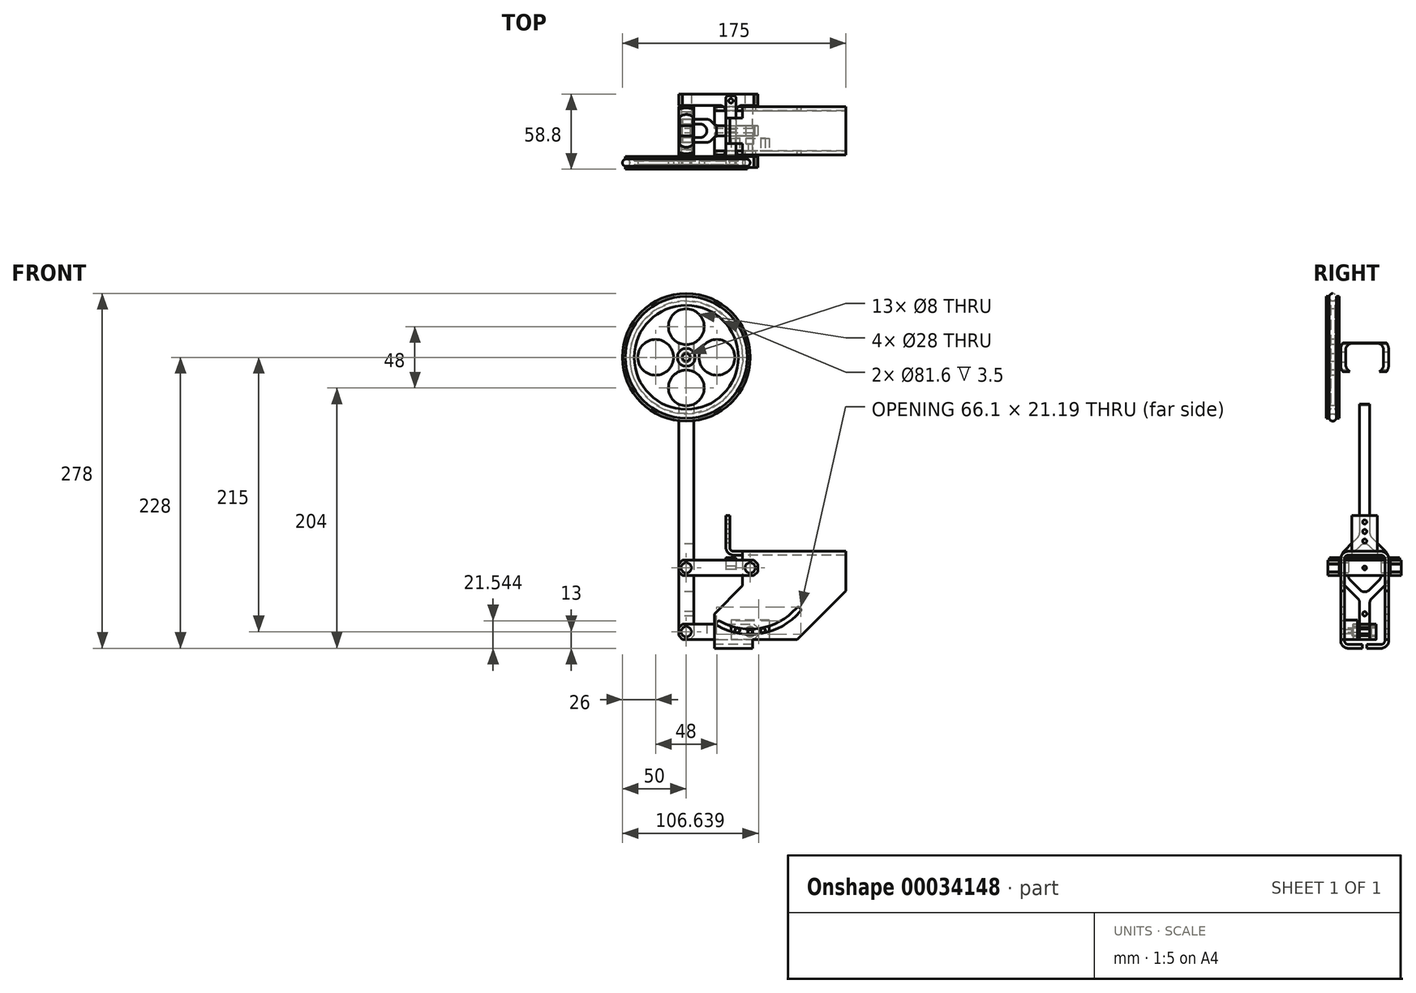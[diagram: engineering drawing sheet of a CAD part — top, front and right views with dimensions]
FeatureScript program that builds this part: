
annotation { "Feature Type Name" : "Feature", "Feature Type Description" : "" }
export const myFeature = defineFeature(function(context is Context, id is Id, definition is map)
    precondition{}
    {
        {
            var Q0;
            Q0=qCreatedBy(makeId("Front.planeOp"),FACE);
            var sketch = newSketch(context, id + "F0", { "sketchPlane" : qUnion([Q0])});
            skLineSegment(sketch, "E0", {"start": v(-68.67, 10) * mm, "end": v(234.98, 10) * mm, "construction": true});
            skLineSegment(sketch, "E1", {"start": v(-69.89, 215) * mm, "end": v(223.35, 215) * mm, "construction": true});
            skLineSegment(sketch, "E2", {"start": v(-65.6, 165) * mm, "end": v(222.13, 165) * mm, "construction": true});
            skLineSegment(sketch, "E3", {"start": v(-66.2, -63) * mm, "end": v(240.7, -63) * mm, "construction": true});
            skSolve(sketch);
        }
        {
            var Q0;
            Q0=sQuery(id+"F0.wireOp",EDGE,"E2");
            cPlane(context, id + "F1", {"entities" : qUnion([Q0]), "cplaneType" : CPlaneType.LINE_ANGLE, "offset" : 370 * mm, "angle" : 90 * degree, "width" : 150 * mm, "height" : 150 * mm});
        }
        {
            var Q0;
            Q0=qCreatedBy(makeId("Right.planeOp"),FACE);
            var sketch = newSketch(context, id + "F2", { "sketchPlane" : qUnion([Q0])});
            skLineSegment(sketch, "E4.bottom", {"start": v(-18.8, 165) * mm, "end": v(18.8, 165) * mm, "construction": true});
            skLineSegment(sketch, "E4.top", {"start": v(-18.8, -50) * mm, "end": v(18.8, -50) * mm, "construction": true});
            skLineSegment(sketch, "E4.left", {"start": v(-18.8, 165) * mm, "end": v(-18.8, -50) * mm, "construction": true});
            skLineSegment(sketch, "E4.right", {"start": v(18.8, 165) * mm, "end": v(18.8, -50) * mm, "construction": true});
            skLineSegment(sketch, "E5", {"start": v(-18.8, 0) * mm, "end": v(18.8, 0) * mm, "construction": true});
            skLineSegment(sketch, "E6", {"start": v(16.16, 152.64) * mm, "end": v(5.46, 141.94) * mm});
            skLineSegment(sketch, "E7", {"start": v(4, 138.4) * mm, "end": v(4, 27.43) * mm});
            skLineSegment(sketch, "E8", {"start": v(5.46, 23.9) * mm, "end": v(15.58, 13.78) * mm});
            skLineSegment(sketch, "E9", {"start": v(18.8, 6) * mm, "end": v(18.8, -6) * mm});
            skLineSegment(sketch, "E10", {"start": v(15.58, -13.78) * mm, "end": v(5.46, -23.9) * mm});
            skLineSegment(sketch, "E11", {"start": v(4, -27.43) * mm, "end": v(4, -50) * mm});
            skLineSegment(sketch, "E12", {"start": v(13.34, 155.46) * mm, "end": v(3.54, 145.66) * mm});
            skLineSegment(sketch, "E13", {"start": v(3.54, 17.34) * mm, "end": v(11.34, 9.54) * mm});
            skLineSegment(sketch, "E14", {"start": v(12.8, 6) * mm, "end": v(12.8, -6) * mm});
            skLineSegment(sketch, "E15", {"start": v(11.34, -9.54) * mm, "end": v(3.54, -17.34) * mm});
            skArc(sketch, "E16.filletArc", {"start": v(13.34, 155.46) * mm, "mid": v(14.42, 157.09) * mm, "end": v(14.8, 159) * mm});
            skPoint(sketch, "E17.visualSharp", {"position": v(18.8, 155.27) * mm});
            skArc(sketch, "E17.filletArc", {"start": v(16.16, 152.64) * mm, "mid": v(18.11, 155.56) * mm, "end": v(18.8, 159) * mm});
            skPoint(sketch, "E18.visualSharp", {"position": v(4, 140.47) * mm});
            skArc(sketch, "E18.filletArc", {"start": v(5.46, 141.94) * mm, "mid": v(4.38, 140.31) * mm, "end": v(4, 138.4) * mm});
            skPoint(sketch, "E19.visualSharp", {"position": v(4, 25.36) * mm});
            skArc(sketch, "E19.filletArc", {"start": v(4, 27.43) * mm, "mid": v(4.38, 25.51) * mm, "end": v(5.46, 23.9) * mm});
            skPoint(sketch, "E20.visualSharp", {"position": v(18.8, 10.56) * mm});
            skArc(sketch, "E20.filletArc", {"start": v(18.8, 6) * mm, "mid": v(17.96, 10.2) * mm, "end": v(15.58, 13.78) * mm});
            skPoint(sketch, "E21.visualSharp", {"position": v(18.8, -10.56) * mm});
            skArc(sketch, "E21.filletArc", {"start": v(15.58, -13.78) * mm, "mid": v(17.96, -10.2) * mm, "end": v(18.8, -6) * mm});
            skPoint(sketch, "E22.visualSharp", {"position": v(4, -25.36) * mm});
            skArc(sketch, "E22.filletArc", {"start": v(5.46, -23.9) * mm, "mid": v(4.38, -25.51) * mm, "end": v(4, -27.43) * mm});
            skPoint(sketch, "E23.visualSharp", {"position": v(12.8, 8.07) * mm});
            skArc(sketch, "E23.filletArc", {"start": v(12.8, 6) * mm, "mid": v(12.42, 7.91) * mm, "end": v(11.34, 9.54) * mm});
            skPoint(sketch, "E24.visualSharp", {"position": v(12.8, -8.07) * mm});
            skArc(sketch, "E24.filletArc", {"start": v(11.34, -9.54) * mm, "mid": v(12.42, -7.91) * mm, "end": v(12.8, -6) * mm});
            skLineSegment(sketch, "E25.MirrorCS", {"start": v(-13.34, 155.46) * mm, "end": v(-3.54, 145.66) * mm});
            skArc(sketch, "E26.MirrorCS", {"start": v(-13.34, 155.46) * mm, "mid": v(-14.42, 157.09) * mm, "end": v(-14.8, 159) * mm});
            skLineSegment(sketch, "E27.MirrorCS", {"start": v(-16.16, 152.64) * mm, "end": v(-5.46, 141.94) * mm});
            skArc(sketch, "E28.MirrorCS", {"start": v(-5.46, 141.94) * mm, "mid": v(-4.38, 140.31) * mm, "end": v(-4, 138.4) * mm});
            skLineSegment(sketch, "E29.MirrorCS", {"start": v(-4, 138.4) * mm, "end": v(-4, 27.43) * mm});
            skArc(sketch, "E30.MirrorCS", {"start": v(-4, 27.43) * mm, "mid": v(-4.38, 25.51) * mm, "end": v(-5.46, 23.9) * mm});
            skLineSegment(sketch, "E31.MirrorCS", {"start": v(-5.46, 23.9) * mm, "end": v(-15.58, 13.78) * mm});
            skArc(sketch, "E32.MirrorCS", {"start": v(-18.8, 6) * mm, "mid": v(-17.96, 10.2) * mm, "end": v(-15.58, 13.78) * mm});
            skLineSegment(sketch, "E33.MirrorCS", {"start": v(-18.8, 6) * mm, "end": v(-18.8, -6) * mm});
            skArc(sketch, "E34.MirrorCS", {"start": v(-15.58, -13.78) * mm, "mid": v(-17.96, -10.2) * mm, "end": v(-18.8, -6) * mm});
            skLineSegment(sketch, "E35.MirrorCS", {"start": v(-15.58, -13.78) * mm, "end": v(-5.46, -23.9) * mm});
            skArc(sketch, "E36.MirrorCS", {"start": v(-5.46, -23.9) * mm, "mid": v(-4.38, -25.51) * mm, "end": v(-4, -27.43) * mm});
            skLineSegment(sketch, "E37.MirrorCS", {"start": v(-4, -27.43) * mm, "end": v(-4, -50) * mm});
            skLineSegment(sketch, "E38.MirrorCS", {"start": v(-11.34, -9.54) * mm, "end": v(-3.54, -17.34) * mm});
            skArc(sketch, "E39.MirrorCS", {"start": v(-11.34, -9.54) * mm, "mid": v(-12.42, -7.91) * mm, "end": v(-12.8, -6) * mm});
            skLineSegment(sketch, "E40.MirrorCS", {"start": v(-12.8, 6) * mm, "end": v(-12.8, -6) * mm});
            skArc(sketch, "E41.MirrorCS", {"start": v(-12.8, 6) * mm, "mid": v(-12.42, 7.91) * mm, "end": v(-11.34, 9.54) * mm});
            skLineSegment(sketch, "E42.MirrorCS", {"start": v(-3.54, 17.34) * mm, "end": v(-11.34, 9.54) * mm});
            skPoint(sketch, "E43.visualSharp", {"position": v(0, 142.13) * mm});
            skArc(sketch, "E43.filletArc", {"start": v(-3.54, 145.66) * mm, "mid": v(0, 144.2) * mm, "end": v(3.54, 145.66) * mm});
            skPoint(sketch, "E44.visualSharp", {"position": v(0, 20.87) * mm});
            skArc(sketch, "E44.filletArc", {"start": v(3.54, 17.34) * mm, "mid": v(0, 18.8) * mm, "end": v(-3.54, 17.34) * mm});
            skPoint(sketch, "E45.visualSharp", {"position": v(0, -20.87) * mm});
            skArc(sketch, "E45.filletArc", {"start": v(-3.54, -17.34) * mm, "mid": v(0, -18.8) * mm, "end": v(3.54, -17.34) * mm});
            skLineSegment(sketch, "E46", {"start": v(4, -50) * mm, "end": v(4, -56) * mm});
            skLineSegment(sketch, "E47", {"start": v(4, -56) * mm, "end": v(0, -56) * mm});
            skLineSegment(sketch, "E48", {"start": v(9.8, 180) * mm, "end": v(0, 180) * mm});
            skLineSegment(sketch, "E49", {"start": v(9.8, 176) * mm, "end": v(0, 176) * mm});
            skLineSegment(sketch, "E50", {"start": v(18.8, 159) * mm, "end": v(18.8, 171) * mm});
            skLineSegment(sketch, "E51", {"start": v(14.8, 171) * mm, "end": v(14.8, 159) * mm});
            skPoint(sketch, "E52.visualSharp", {"position": v(14.8, 176) * mm});
            skArc(sketch, "E52.filletArc", {"start": v(14.8, 171) * mm, "mid": v(13.34, 174.54) * mm, "end": v(9.8, 176) * mm});
            skPoint(sketch, "E53.visualSharp", {"position": v(18.8, 180) * mm});
            skArc(sketch, "E53.filletArc", {"start": v(18.8, 171) * mm, "mid": v(16.16, 177.36) * mm, "end": v(9.8, 180) * mm});
            skLineSegment(sketch, "E54.MirrorCS", {"start": v(-14.8, 171) * mm, "end": v(-14.8, 159) * mm});
            skArc(sketch, "E55.MirrorCS", {"start": v(-14.8, 171) * mm, "mid": v(-13.34, 174.54) * mm, "end": v(-9.8, 176) * mm});
            skLineSegment(sketch, "E56.MirrorCS", {"start": v(-9.8, 176) * mm, "end": v(0, 176) * mm});
            skArc(sketch, "E57.MirrorCS", {"start": v(-16.16, 152.64) * mm, "mid": v(-18.11, 155.56) * mm, "end": v(-18.8, 159) * mm});
            skLineSegment(sketch, "E58.MirrorCS", {"start": v(-18.8, 159) * mm, "end": v(-18.8, 171) * mm});
            skArc(sketch, "E59.MirrorCS", {"start": v(-18.8, 171) * mm, "mid": v(-16.16, 177.36) * mm, "end": v(-9.8, 180) * mm});
            skLineSegment(sketch, "E60.MirrorCS", {"start": v(-9.8, 180) * mm, "end": v(0, 180) * mm});
            skLineSegment(sketch, "E61.MirrorCS", {"start": v(-4, -50) * mm, "end": v(-4, -56) * mm});
            skLineSegment(sketch, "E62.MirrorCS", {"start": v(-4, -56) * mm, "end": v(0, -56) * mm});
            skCircle(sketch, "E63", {"center": v(0, -36) * mm, "radius": 1.65 * mm});
            skSolve(sketch);
        }
        {
            var Q0;
            Q0 = qSketchRegion(id + "F2", true);
            extrude(context, id + "F3", {"entities" : qUnion([Q0]), "endBound" : BoundingType.SYMMETRIC, "depth" : 12 * mm});
        }
        {
            var Q0;
            Q0=makeQuery(id+"F3.opExtrude","CAP_EDGE",EDGE,{"disambiguationData":[OSD([sQuery(id+"F2.wireOp",EDGE,"E47"),sQuery(id+"F2.wireOp",EDGE,"E62.MirrorCS")])],"isStart":false});
            var Q1;
            Q1=makeQuery(id+"F3.opExtrude","CAP_EDGE",EDGE,{"disambiguationData":[OSD([sQuery(id+"F2.wireOp",EDGE,"E47"),sQuery(id+"F2.wireOp",EDGE,"E62.MirrorCS")])],"isStart":true});
            chamfer(context, id + "F4", {"entities" : qUnion([Q0, Q1]), "width" : 3 * mm, "tangentPropagation" : true});
        }
        {
            var Q0;
            Q0=qCreatedBy(makeId("Top.planeOp"),FACE);
            var sketch = newSketch(context, id + "F5", { "sketchPlane" : qUnion([Q0])});
            skLineSegment(sketch, "E64", {"start": v(-6, 28.8) * mm, "end": v(-6, 20) * mm});
            skLineSegment(sketch, "E65", {"start": v(-6, 20) * mm, "end": v(26, 20) * mm});
            skLineSegment(sketch, "E66", {"start": v(-6, 28.8) * mm, "end": v(31, 28.8) * mm});
            skLineSegment(sketch, "E67", {"start": v(44, 28.8) * mm, "end": v(56, 28.8) * mm});
            skLineSegment(sketch, "E68", {"start": v(56, 28.8) * mm, "end": v(56, 20) * mm});
            skLineSegment(sketch, "E69", {"start": v(56, 20) * mm, "end": v(44, 20) * mm});
            skLineSegment(sketch, "E70", {"start": v(50, 28.8) * mm, "end": v(50, 20) * mm, "construction": true});
            skLineSegment(sketch, "E71", {"start": v(31, 28.8) * mm, "end": v(44, 28.8) * mm});
            skLineSegment(sketch, "E72", {"start": v(39, 15) * mm, "end": v(39, 0) * mm});
            skPoint(sketch, "E73.visualSharp", {"position": v(39, 20) * mm});
            skArc(sketch, "E73.filletArc", {"start": v(44, 20) * mm, "mid": v(40.46, 18.54) * mm, "end": v(39, 15) * mm});
            skLineSegment(sketch, "E74.MirrorCS", {"start": v(-6, -28.8) * mm, "end": v(-6, -20) * mm});
            skLineSegment(sketch, "E75.MirrorCS", {"start": v(-6, -28.8) * mm, "end": v(31, -28.8) * mm});
            skLineSegment(sketch, "E76.MirrorCS", {"start": v(31, -28.8) * mm, "end": v(44, -28.8) * mm});
            skLineSegment(sketch, "E77.MirrorCS", {"start": v(44, -28.8) * mm, "end": v(56, -28.8) * mm});
            skLineSegment(sketch, "E78.MirrorCS", {"start": v(56, -28.8) * mm, "end": v(56, -20) * mm});
            skLineSegment(sketch, "E79.MirrorCS", {"start": v(56, -20) * mm, "end": v(44, -20) * mm});
            skArc(sketch, "E80.MirrorCS", {"start": v(44, -20) * mm, "mid": v(40.46, -18.54) * mm, "end": v(39, -15) * mm});
            skLineSegment(sketch, "E81.MirrorCS", {"start": v(39, -15) * mm, "end": v(39, 0) * mm});
            skLineSegment(sketch, "E82", {"start": v(31, 15) * mm, "end": v(31, 0) * mm});
            skPoint(sketch, "E83.visualSharp", {"position": v(31, 20) * mm});
            skArc(sketch, "E83.filletArc", {"start": v(31, 15) * mm, "mid": v(29.54, 18.54) * mm, "end": v(26, 20) * mm});
            skLineSegment(sketch, "E84.MirrorCS", {"start": v(31, -15) * mm, "end": v(31, 0) * mm});
            skArc(sketch, "E85.MirrorCS", {"start": v(31, -15) * mm, "mid": v(29.54, -18.54) * mm, "end": v(26, -20) * mm});
            skLineSegment(sketch, "E86.MirrorCS", {"start": v(-6, -20) * mm, "end": v(26, -20) * mm});
            skSolve(sketch);
        }
        {
            var Q0;
            Q0 = qSketchRegion(id + "F5", true);
            extrude(context, id + "F6", {"entities" : qUnion([Q0]), "endBound" : BoundingType.SYMMETRIC, "depth" : 12 * mm});
        }
        {
            var Q0;
            Q0=makeQuery(id+"F6.opExtrude","CAP_EDGE",EDGE,{"disambiguationData":[OSD([sQuery(id+"F5.wireOp",EDGE,"E78.MirrorCS")])],"isStart":false});
            var Q1;
            Q1=makeQuery(id+"F6.opExtrude","CAP_EDGE",EDGE,{"disambiguationData":[OSD([sQuery(id+"F5.wireOp",EDGE,"E78.MirrorCS")])],"isStart":true});
            var Q2;
            Q2=makeQuery(id+"F6.opExtrude","CAP_EDGE",EDGE,{"disambiguationData":[OSD([sQuery(id+"F5.wireOp",EDGE,"E68")])],"isStart":false});
            var Q3;
            Q3=makeQuery(id+"F6.opExtrude","CAP_EDGE",EDGE,{"disambiguationData":[OSD([sQuery(id+"F5.wireOp",EDGE,"E68")])],"isStart":true});
            var Q4;
            Q4=makeQuery(id+"F6.opExtrude","CAP_EDGE",EDGE,{"disambiguationData":[OSD([sQuery(id+"F5.wireOp",EDGE,"E74.MirrorCS")])],"isStart":false});
            var Q5;
            Q5=makeQuery(id+"F6.opExtrude","CAP_EDGE",EDGE,{"disambiguationData":[OSD([sQuery(id+"F5.wireOp",EDGE,"E74.MirrorCS")])],"isStart":true});
            var Q6;
            Q6=makeQuery(id+"F6.opExtrude","CAP_EDGE",EDGE,{"disambiguationData":[OSD([sQuery(id+"F5.wireOp",EDGE,"E64")])],"isStart":false});
            var Q7;
            Q7=makeQuery(id+"F6.opExtrude","CAP_EDGE",EDGE,{"disambiguationData":[OSD([sQuery(id+"F5.wireOp",EDGE,"E64")])],"isStart":true});
            chamfer(context, id + "F7", {"entities" : qUnion([Q0, Q1, Q2, Q3, Q4, Q5, Q6, Q7]), "width" : 3 * mm, "tangentPropagation" : true});
        }
        {
            var Q0;
            Q0=qCreatedBy(makeId("Top.planeOp"),FACE);
            cPlane(context, id + "F8", {"entities" : qUnion([Q0]), "cplaneType" : CPlaneType.OFFSET, "offset" : 50 * mm, "oppositeDirection" : true, "width" : 150 * mm, "height" : 150 * mm});
        }
        {
            var Q0;
            Q0=qCreatedBy(id+"F8.planeOp",FACE);
            var sketch = newSketch(context, id + "F9", { "sketchPlane" : qUnion([Q0])});
            skLineSegment(sketch, "E87.top", {"start": v(-6, -5.2) * mm, "end": v(11, -5.2) * mm});
            skLineSegment(sketch, "E87.left", {"start": v(-6, -9) * mm, "end": v(-6, -5.2) * mm});
            skLineSegment(sketch, "E88", {"start": v(16, -0.2) * mm, "end": v(16, 0) * mm});
            skLineSegment(sketch, "E89", {"start": v(-6, -9) * mm, "end": v(16, -9) * mm});
            skLineSegment(sketch, "E90", {"start": v(19.54, -7.54) * mm, "end": v(21.6, -5.46) * mm});
            skLineSegment(sketch, "E91", {"start": v(25.14, -4) * mm, "end": v(56, -4) * mm});
            skLineSegment(sketch, "E92", {"start": v(56, -4) * mm, "end": v(56, 0) * mm});
            skPoint(sketch, "E93.visualSharp", {"position": v(16, -5.2) * mm});
            skArc(sketch, "E93.filletArc", {"start": v(11, -5.2) * mm, "mid": v(14.54, -3.74) * mm, "end": v(16, -0.2) * mm});
            skPoint(sketch, "E94.visualSharp", {"position": v(18.07, -9) * mm});
            skArc(sketch, "E94.filletArc", {"start": v(16, -9) * mm, "mid": v(17.91, -8.62) * mm, "end": v(19.54, -7.54) * mm});
            skPoint(sketch, "E95.visualSharp", {"position": v(23.07, -4) * mm});
            skArc(sketch, "E95.filletArc", {"start": v(25.14, -4) * mm, "mid": v(23.23, -4.38) * mm, "end": v(21.6, -5.46) * mm});
            skLineSegment(sketch, "E96.MirrorCS", {"start": v(16, 0.2) * mm, "end": v(16, 0) * mm});
            skArc(sketch, "E97.MirrorCS", {"start": v(11, 5.2) * mm, "mid": v(14.54, 3.74) * mm, "end": v(16, 0.2) * mm});
            skLineSegment(sketch, "E98.MirrorCS", {"start": v(-6, 5.2) * mm, "end": v(11, 5.2) * mm});
            skLineSegment(sketch, "E99.MirrorCS", {"start": v(-6, 9) * mm, "end": v(-6, 5.2) * mm});
            skLineSegment(sketch, "E100.MirrorCS", {"start": v(-6, 9) * mm, "end": v(16, 9) * mm});
            skArc(sketch, "E101.MirrorCS", {"start": v(16, 9) * mm, "mid": v(17.91, 8.62) * mm, "end": v(19.54, 7.54) * mm});
            skLineSegment(sketch, "E102.MirrorCS", {"start": v(19.54, 7.54) * mm, "end": v(21.6, 5.46) * mm});
            skArc(sketch, "E103.MirrorCS", {"start": v(25.14, 4) * mm, "mid": v(23.23, 4.38) * mm, "end": v(21.6, 5.46) * mm});
            skLineSegment(sketch, "E104.MirrorCS", {"start": v(25.14, 4) * mm, "end": v(56, 4) * mm});
            skLineSegment(sketch, "E105.MirrorCS", {"start": v(56, 4) * mm, "end": v(56, 0) * mm});
            skSolve(sketch);
        }
        {
            var Q0;
            Q0 = qSketchRegion(id + "F9", true);
            extrude(context, id + "F10", {"entities" : qUnion([Q0]), "endBound" : BoundingType.SYMMETRIC, "depth" : 12 * mm});
        }
        {
            var Q0;
            Q0=makeQuery(id+"F10.opExtrude","CAP_EDGE",EDGE,{"disambiguationData":[OSD([sQuery(id+"F9.wireOp",EDGE,"E87.left")])],"isStart":true});
            var Q1;
            Q1=makeQuery(id+"F10.opExtrude","CAP_EDGE",EDGE,{"disambiguationData":[OSD([sQuery(id+"F9.wireOp",EDGE,"E87.left")])],"isStart":false});
            var Q2;
            Q2=makeQuery(id+"F10.opExtrude","CAP_EDGE",EDGE,{"disambiguationData":[OSD([sQuery(id+"F9.wireOp",EDGE,"E87.right")])],"isStart":true});
            var Q3;
            Q3=makeQuery(id+"F10.opExtrude","CAP_EDGE",EDGE,{"disambiguationData":[OSD([sQuery(id+"F9.wireOp",EDGE,"E87.right")])],"isStart":false});
            var Q4;
            Q4=makeQuery(id+"F10.opExtrude","CAP_EDGE",EDGE,{"disambiguationData":[OSD([sQuery(id+"F9.wireOp",EDGE,"E99.MirrorCS")])],"isStart":true});
            var Q5;
            Q5=makeQuery(id+"F10.opExtrude","CAP_EDGE",EDGE,{"disambiguationData":[OSD([sQuery(id+"F9.wireOp",EDGE,"E99.MirrorCS")])],"isStart":false});
            var Q6;
            Q6=makeQuery(id+"F10.opExtrude","CAP_EDGE",EDGE,{"disambiguationData":[OSD([sQuery(id+"F9.wireOp",EDGE,"E92"),sQuery(id+"F9.wireOp",EDGE,"E105.MirrorCS")])],"isStart":true});
            var Q7;
            Q7=makeQuery(id+"F10.opExtrude","CAP_EDGE",EDGE,{"disambiguationData":[OSD([sQuery(id+"F9.wireOp",EDGE,"E92"),sQuery(id+"F9.wireOp",EDGE,"E105.MirrorCS")])],"isStart":false});
            chamfer(context, id + "F11", {"entities" : qUnion([Q0, Q1, Q2, Q3, Q4, Q5, Q6, Q7]), "width" : 3 * mm, "tangentPropagation" : true});
        }
        {
            var Q0;
            Q0=qCreatedBy(makeId("Front.planeOp"),FACE);
            var sketch = newSketch(context, id + "F12", { "sketchPlane" : qUnion([Q0])});
            skCircle(sketch, "E106", {"center": v(0, 0) * mm, "radius": 4 * mm});
            skCircle(sketch, "E107", {"center": v(0, -50) * mm, "radius": 4 * mm});
            skCircle(sketch, "E108", {"center": v(0, 165) * mm, "radius": 4 * mm});
            skCircle(sketch, "E109", {"center": v(50, 0) * mm, "radius": 4 * mm});
            skCircle(sketch, "E110", {"center": v(50, -50) * mm, "radius": 4 * mm});
            skSolve(sketch);
        }
        {
            var Q0;
            Q0 = qSketchRegion(id + "F12", true);
            extrude(context, id + "F13", {"entities" : qUnion([Q0]), "operationType" : NewBodyOperationType.REMOVE, "endBound" : BoundingType.THROUGH_ALL, "oppositeDirection" : true, "depth" : 25 * mm, "hasSecondDirection" : true, "secondDirectionBound" : SecondDirectionBoundingType.THROUGH_ALL, "secondDirectionOppositeDirection" : false, "secondDirectionDepth" : 25 * mm});
        }
        {
            var Q0;
            Q0=qCreatedBy(makeId("Front.planeOp"),FACE);
            var sketch = newSketch(context, id + "F14", { "sketchPlane" : qUnion([Q0])});
            skLineSegment(sketch, "E111", {"start": v(44, 13) * mm, "end": v(44, -14) * mm});
            skLineSegment(sketch, "E112", {"start": v(44, -14) * mm, "end": v(22, -36) * mm});
            skLineSegment(sketch, "E113", {"start": v(22, -36) * mm, "end": v(22, -56) * mm});
            skLineSegment(sketch, "E114", {"start": v(22, -56) * mm, "end": v(87, -56) * mm});
            skLineSegment(sketch, "E115", {"start": v(125, -18) * mm, "end": v(125, 13) * mm});
            skLineSegment(sketch, "E116", {"start": v(125, 13) * mm, "end": v(44, 13) * mm});
            skLineSegment(sketch, "E117", {"start": v(87, -56) * mm, "end": v(125, -18) * mm});
            skPoint(sketch, "E118.orphan", {"position": v(125, -56) * mm});
            skSolve(sketch);
        }
        {
            var Q0;
            Q0 = qSketchRegion(id + "F14", true);
            extrude(context, id + "F15", {"entities" : qUnion([Q0]), "endBound" : BoundingType.SYMMETRIC, "depth" : 37.6 * mm});
        }
        {
            var Q0;
            Q0=makeQuery(id+"F15.opExtrude","SWEPT_FACE",FACE,{"disambiguationData":[OSD([sQuery(id+"F14.wireOp",EDGE,"E114")])]});
            var Q1;
            Q1=makeQuery(id+"F15.opExtrude","SWEPT_FACE",FACE,{"disambiguationData":[OSD([sQuery(id+"F14.wireOp",EDGE,"E113")])]});
            var Q2;
            Q2=makeQuery(id+"F15.opExtrude","SWEPT_FACE",FACE,{"disambiguationData":[OSD([sQuery(id+"F14.wireOp",EDGE,"E112")])]});
            var Q3;
            Q3=makeQuery(id+"F15.opExtrude","SWEPT_FACE",FACE,{"disambiguationData":[OSD([sQuery(id+"F14.wireOp",EDGE,"E111")])]});
            var Q4;
            Q4=makeQuery(id+"F15.opExtrude","SWEPT_FACE",FACE,{"disambiguationData":[OSD([sQuery(id+"F14.wireOp",EDGE,"E115")])]});
            var Q5;
            Q5=makeQuery(id+"F15.opExtrude","SWEPT_FACE",FACE,{"disambiguationData":[OSD([sQuery(id+"F14.wireOp",EDGE,"E117")])]});
            var Q6;
            Q6=makeQuery(id+"F15.opExtrude","SWEPT_FACE",FACE,{"disambiguationData":[OSD([sQuery(id+"F14.wireOp",EDGE,"f684425a-3b98-4159-92de-e356273894e7")])]});
            shell(context, id + "F16", {"entities" : qUnion([Q0, Q1, Q2, Q3, Q4, Q5, Q6]), "thickness" : 3 * mm});
        }
        {
            var Q0;
            Q0=makeQuery(id+"F15.opExtrude","CAP_FACE",FACE,{"disambiguationData":[OSD([sQuery(id+"F14.wireOp",EDGE,"E111"),sQuery(id+"F14.wireOp",EDGE,"E112"),sQuery(id+"F14.wireOp",EDGE,"E113"),sQuery(id+"F14.wireOp",EDGE,"E114"),sQuery(id+"F14.wireOp",EDGE,"E115"),sQuery(id+"F14.wireOp",EDGE,"E116")])],"isStart":false});
            var sketch = newSketch(context, id + "F17", { "sketchPlane" : qUnion([Q0])});
            skCircle(sketch, "E119", {"center": v(0, 0) * mm, "radius": 165 * mm, "construction": true});
            skPoint(sketch, "E120", {"position": v(0, 165) * mm});
            skLineSegment(sketch, "E121", {"start": v(50, 157.24) * mm, "end": v(50, -157.24) * mm, "construction": true});
            skPoint(sketch, "E122", {"position": v(50, 0) * mm});
            skLineSegment(sketch, "E123", {"start": v(50, 157.24) * mm, "end": v(-50, -157.24) * mm, "construction": true});
            skLineSegment(sketch, "E124", {"start": v(93.28, 136.1) * mm, "end": v(-2.46, -164.98) * mm, "construction": true});
            skLineSegment(sketch, "E125", {"start": v(-100, 131.24) * mm, "end": v(100, -131.24) * mm, "construction": true});
            skLineSegment(sketch, "E126", {"start": v(-65.42, 151.48) * mm, "end": v(128.69, -103.27) * mm, "construction": true});
            skCircle(sketch, "E127", {"center": v(50, 0) * mm, "radius": 50 * mm, "construction": true});
            skSolve(sketch);
        }
        {
            var Q0;
            Q0=makeQuery(id+"F17.imprint","IMPRINT",FACE,{"disambiguationData":[TD([[makeQuery(id+"F17.imprint","IMPRINT",EDGE,{"derivedFrom":makeQuery(id+"F15.opExtrude","CAP_EDGE",EDGE,{"disambiguationData":[OSD([sQuery(id+"F14.wireOp",EDGE,"E111")])],"isStart":false})}),1.0]])]});
            var sketch = newSketch(context, id + "F18", { "sketchPlane" : qUnion([Q0])});
            skPoint(sketch, "E128", {"position": v(25.62, -43.66) * mm});
            skPoint(sketch, "E129", {"position": v(87.64, -32.9) * mm});
            skArc(sketch, "E130", {"start": v(25.62, -43.66) * mm, "mid": v(58.54, -49.27) * mm, "end": v(87.64, -32.9) * mm, "construction": true});
            skArc(sketch, "E131.0.startCap", {"start": v(24.63, -45.45) * mm, "mid": v(23.83, -42.66) * mm, "end": v(26.62, -41.87) * mm});
            skArc(sketch, "E131.0.endCap", {"start": v(86.1, -31.56) * mm, "mid": v(89, -31.36) * mm, "end": v(89.19, -34.26) * mm});
            skArc(sketch, "E131.0.left", {"start": v(26.62, -41.87) * mm, "mid": v(58.19, -47.25) * mm, "end": v(86.1, -31.56) * mm});
            skArc(sketch, "E131.0.right", {"start": v(24.63, -45.45) * mm, "mid": v(58.89, -51.29) * mm, "end": v(89.19, -34.26) * mm});
            skCircle(sketch, "E132", {"center": v(50, 0) * mm, "radius": 4 * mm});
            skSolve(sketch);
        }
        {
            var Q0;
            Q0 = qSketchRegion(id + "F18", true);
            extrude(context, id + "F19", {"entities" : qUnion([Q0]), "operationType" : NewBodyOperationType.REMOVE, "endBound" : BoundingType.THROUGH_ALL, "oppositeDirection" : true, "depth" : 25 * mm});
        }
        {
            var Q0;
            {var subQ0=sQuery(id+"F14.wireOp",EDGE,"E111");var subQ1=sQuery(id+"F14.wireOp",EDGE,"E112");var subQ2=sQuery(id+"F14.wireOp",EDGE,"E113");var subQ3=sQuery(id+"F14.wireOp",EDGE,"E114");var subQ4=sQuery(id+"F14.wireOp",EDGE,"E115");var subQ5=sQuery(id+"F14.wireOp",EDGE,"E116");Q0=makeQuery(id+"F16.opShell","OFFSET_FACE",FACE,{"disambiguationData":[OSD([subQ0,subQ1,subQ2,subQ3,subQ4,subQ5]),TDD([makeQuery(id+"F15.opExtrude","CAP_FACE",FACE,{"disambiguationData":[OSD([subQ0,subQ1,subQ2,subQ3,subQ4,subQ5])],"isStart":false})])]});}
            var sketch = newSketch(context, id + "F20", { "sketchPlane" : qUnion([Q0])});
            skLineSegment(sketch, "E133.bottom", {"start": v(-65, -41) * mm, "end": v(-35, -41) * mm});
            skLineSegment(sketch, "E133.top", {"start": v(-65, -56) * mm, "end": v(-35, -56) * mm});
            skLineSegment(sketch, "E133.left", {"start": v(-65, -41) * mm, "end": v(-65, -56) * mm});
            skLineSegment(sketch, "E133.right", {"start": v(-35, -41) * mm, "end": v(-35, -56) * mm});
            skLineSegment(sketch, "E134", {"start": v(-50, -56) * mm, "end": v(-50, -50) * mm, "construction": true});
            skSolve(sketch);
        }
        {
            var Q0;
            Q0 = qSketchRegion(id + "F20", true);
            extrude(context, id + "F21", {"entities" : qUnion([Q0]), "operationType" : NewBodyOperationType.ADD, "depth" : 10 * mm});
        }
        {
            var Q0;
            Q0=makeQuery(id+"F21.opExtrude","CAP_FACE",FACE,{"disambiguationData":[OSD([sQuery(id+"F20.wireOp",EDGE,"E133.bottom"),sQuery(id+"F20.wireOp",EDGE,"E133.top"),sQuery(id+"F20.wireOp",EDGE,"E133.left"),sQuery(id+"F20.wireOp",EDGE,"E133.right")])],"isStart":false});
            var sketch = newSketch(context, id + "F22", { "sketchPlane" : qUnion([Q0])});
            skCircle(sketch, "E135", {"center": v(-50, -50) * mm, "radius": 3 * mm});
            skSolve(sketch);
        }
        {
            var Q0;
            Q0 = qSketchRegion(id + "F22", true);
            extrude(context, id + "F23", {"entities" : qUnion([Q0]), "operationType" : NewBodyOperationType.REMOVE, "oppositeDirection" : true, "depth" : 4.4 * mm});
        }
        {
            var Q0;
            Q0=makeQuery(id+"F21.opExtrude","CAP_FACE",FACE,{"disambiguationData":[OSD([sQuery(id+"F20.wireOp",EDGE,"E133.bottom"),sQuery(id+"F20.wireOp",EDGE,"E133.top"),sQuery(id+"F20.wireOp",EDGE,"E133.left"),sQuery(id+"F20.wireOp",EDGE,"E133.right")])],"isStart":true});
            var sketch = newSketch(context, id + "F24", { "sketchPlane" : qUnion([Q0])});
            skCircle(sketch, "E136", {"center": v(50, -50) * mm, "radius": 1.65 * mm});
            skCircle(sketch, "E137", {"center": v(60, -49) * mm, "radius": 1.65 * mm});
            skCircle(sketch, "E138", {"center": v(40, -49) * mm, "radius": 1.65 * mm});
            skLineSegment(sketch, "E139", {"start": v(40, -49) * mm, "end": v(60, -49) * mm, "construction": true});
            skSolve(sketch);
        }
        {
            var Q0;
            Q0 = qSketchRegion(id + "F24", true);
            extrude(context, id + "F25", {"entities" : qUnion([Q0]), "operationType" : NewBodyOperationType.REMOVE, "endBound" : BoundingType.THROUGH_ALL, "oppositeDirection" : true, "depth" : 25 * mm});
        }
        {
            var Q0;
            Q0=makeQuery(id+"F21.opExtrude","CAP_FACE",FACE,{"disambiguationData":[OSD([sQuery(id+"F20.wireOp",EDGE,"E133.bottom"),sQuery(id+"F20.wireOp",EDGE,"E133.top"),sQuery(id+"F20.wireOp",EDGE,"E133.left"),sQuery(id+"F20.wireOp",EDGE,"E133.right")])],"isStart":true});
            var sketch = newSketch(context, id + "F26", { "sketchPlane" : qUnion([Q0])});
            skCircle(sketch, "E140", {"center": v(40, -49) * mm, "radius": 2 * mm});
            skCircle(sketch, "E141", {"center": v(50, -50) * mm, "radius": 2 * mm});
            skCircle(sketch, "E142", {"center": v(60, -49) * mm, "radius": 2 * mm});
            skSolve(sketch);
        }
        {
            var Q0;
            Q0 = qSketchRegion(id + "F26", true);
            extrude(context, id + "F27", {"entities" : qUnion([Q0]), "operationType" : NewBodyOperationType.REMOVE, "oppositeDirection" : true, "depth" : 0.1 * mm});
        }
        {
            var Q0;
            Q0=makeQuery(id+"F21.opExtrude","CAP_FACE",FACE,{"disambiguationData":[OSD([sQuery(id+"F20.wireOp",EDGE,"E133.bottom"),sQuery(id+"F20.wireOp",EDGE,"E133.top"),sQuery(id+"F20.wireOp",EDGE,"E133.left"),sQuery(id+"F20.wireOp",EDGE,"E133.right")])],"isStart":false});
            var sketch = newSketch(context, id + "F28", { "sketchPlane" : qUnion([Q0])});
            skCircle(sketch, "E143", {"center": v(-60, -49) * mm, "radius": 2 * mm});
            skCircle(sketch, "E144", {"center": v(-40, -49) * mm, "radius": 2 * mm});
            skSolve(sketch);
        }
        {
            var Q0;
            Q0 = qSketchRegion(id + "F28", true);
            extrude(context, id + "F29", {"entities" : qUnion([Q0]), "operationType" : NewBodyOperationType.REMOVE, "oppositeDirection" : true, "depth" : 0.1 * mm});
        }
        {
            var Q0;
            Q0=makeQuery(id+"F23.boolean.opBoolean","COPY",FACE,{"derivedFrom":makeQuery(id+"F23.opExtrude","CAP_FACE",FACE,{"disambiguationData":[OSD([sQuery(id+"F22.wireOp",EDGE,"E135")])],"isStart":false})});
            var sketch = newSketch(context, id + "F30", { "sketchPlane" : qUnion([Q0])});
            skCircle(sketch, "E145", {"center": v(-50, -50) * mm, "radius": 2 * mm});
            skSolve(sketch);
        }
        {
            var Q0;
            Q0 = qSketchRegion(id + "F30", true);
            extrude(context, id + "F31", {"entities" : qUnion([Q0]), "operationType" : NewBodyOperationType.REMOVE, "oppositeDirection" : true, "depth" : 0.1 * mm});
        }
        {
            var Q0;
            {var subQ0=makeQuery(id+"F15.opExtrude","CAP_EDGE",EDGE,{"disambiguationData":[OSD([sQuery(id+"F14.wireOp",EDGE,"E116")])],"isStart":false});Q0=makeQuery(id+"FbJh5xUGn1YsbCO_5.boolean.opBoolean","MERGE",EDGE,{"derivedFrom":[subQ0,makeQuery(id+"FbJh5xUGn1YsbCO_5.opPattern","COPY",EDGE,{"derivedFrom":subQ0,"instanceName":"1"})]});}
            var Q1;
            {var subQ0=makeQuery(id+"F15.opExtrude","CAP_EDGE",EDGE,{"disambiguationData":[OSD([sQuery(id+"F14.wireOp",EDGE,"E116")])],"isStart":true});Q1=makeQuery(id+"FbJh5xUGn1YsbCO_5.boolean.opBoolean","MERGE",EDGE,{"derivedFrom":[subQ0,makeQuery(id+"FbJh5xUGn1YsbCO_5.opPattern","COPY",EDGE,{"derivedFrom":subQ0,"instanceName":"1"})]});}
            fillet(context, id + "F32", {"entities" : qUnion([Q0, Q1]), "radius" : 6 * mm, "tangentPropagation" : true, "allowEdgeOverflow" : false});
        }
        {
            var Q0;
            {var subQ0=sQuery(id+"F14.wireOp",EDGE,"E116");var subQ1=makeQuery(id+"F16.opShell","OFFSET_EDGE",EDGE,{"disambiguationData":[OSD([subQ0]),TDD([makeQuery(id+"F15.opExtrude","CAP_EDGE",EDGE,{"disambiguationData":[OSD([subQ0])],"isStart":false})])]});Q0=makeQuery(id+"FbJh5xUGn1YsbCO_5.boolean.opBoolean","MERGE",EDGE,{"derivedFrom":[subQ1,makeQuery(id+"FbJh5xUGn1YsbCO_5.opPattern","COPY",EDGE,{"derivedFrom":subQ1,"instanceName":"1"})]});}
            var Q1;
            {var subQ0=sQuery(id+"F14.wireOp",EDGE,"E116");var subQ1=makeQuery(id+"F16.opShell","OFFSET_EDGE",EDGE,{"disambiguationData":[OSD([subQ0]),TDD([makeQuery(id+"F15.opExtrude","CAP_EDGE",EDGE,{"disambiguationData":[OSD([subQ0])],"isStart":true})])]});Q1=makeQuery(id+"FbJh5xUGn1YsbCO_5.boolean.opBoolean","MERGE",EDGE,{"derivedFrom":[subQ1,makeQuery(id+"FbJh5xUGn1YsbCO_5.opPattern","COPY",EDGE,{"derivedFrom":subQ1,"instanceName":"1"})]});}
            fillet(context, id + "F33", {"entities" : qUnion([Q0, Q1]), "radius" : 3 * mm, "tangentPropagation" : true, "allowEdgeOverflow" : false});
        }
        {
            var Q0;
            Q0=qCreatedBy(id+"F1.planeOp",FACE);
            var sketch = newSketch(context, id + "F34", { "sketchPlane" : qUnion([Q0])});
            skLineSegment(sketch, "E146", {"start": v(3, -20) * mm, "end": v(7, -20) * mm});
            skLineSegment(sketch, "E147", {"start": v(7, -20) * mm, "end": v(7, -23.5) * mm});
            skLineSegment(sketch, "E148", {"start": v(7, -23.5) * mm, "end": v(40.8, -23.5) * mm});
            skLineSegment(sketch, "E149", {"start": v(40.8, -23.5) * mm, "end": v(40.8, -20) * mm});
            skLineSegment(sketch, "E150", {"start": v(40.8, -20) * mm, "end": v(47.8, -20) * mm});
            skLineSegment(sketch, "E151", {"start": v(47.8, -20) * mm, "end": v(47.8, -22.15) * mm});
            skLineSegment(sketch, "E152", {"start": v(47.8, -22.15) * mm, "end": v(44.3, -22.15) * mm});
            skLineSegment(sketch, "E153", {"start": v(44.3, -22.15) * mm, "end": v(44.3, -27.85) * mm});
            skLineSegment(sketch, "E154", {"start": v(44.3, -27.85) * mm, "end": v(47.8, -27.85) * mm});
            skLineSegment(sketch, "E155", {"start": v(47.8, -27.85) * mm, "end": v(47.8, -30) * mm});
            skLineSegment(sketch, "E156", {"start": v(47.8, -30) * mm, "end": v(40.8, -30) * mm});
            skLineSegment(sketch, "E157", {"start": v(40.8, -30) * mm, "end": v(40.8, -26.5) * mm});
            skLineSegment(sketch, "E158", {"start": v(40.8, -26.5) * mm, "end": v(7, -26.5) * mm});
            skLineSegment(sketch, "E159", {"start": v(7, -26.5) * mm, "end": v(7, -30) * mm});
            skLineSegment(sketch, "E160", {"start": v(7, -30) * mm, "end": v(3, -30) * mm});
            skLineSegment(sketch, "E161", {"start": v(3, -30) * mm, "end": v(3, -20) * mm});
            skLineSegment(sketch, "E162", {"start": v(0, -20) * mm, "end": v(0, -30) * mm, "construction": true});
            skCircle(sketch, "E163", {"center": v(47.15, -25) * mm, "radius": 2.85 * mm});
            skSolve(sketch);
        }
        {
            var Q0;
            Q0=makeQuery(id+"F34.imprint","IMPRINT",FACE,{"disambiguationData":[TD([[makeQuery(id+"F34.imprint","IMPRINT",EDGE,{"derivedFrom":sQuery(id+"F34.wireOp",EDGE,"E146")}),-1.0]])]});
            var Q1;
            {var subQ0=sQuery(id+"F34.wireOp",EDGE,"E163");var subQ2=makeQuery(id+"F34.imprint","INTERSECT",VERTEX,{"derivedFrom":[sQuery(id+"F34.wireOp",EDGE,"E152"),subQ0]});Q1=makeQuery(id+"F34.imprint","IMPRINT",FACE,{"disambiguationData":[TD([[makeQuery(id+"F34.imprint","IMPRINT",EDGE,{"disambiguationData":[TD([[subQ2,-1.0]])],"derivedFrom":subQ0}),1.0]])]});}
            var Q2;
            Q2=sQuery(id+"F34.wireOp",EDGE,"E162");
            revolve(context, id + "F35", {"entities" : qUnion([Q0, Q1]), "axis" : qUnion([Q2]), "revolveType" : RevolveType.FULL});
        }
        {
            var Q0;
            Q0=makeQuery(id+"F35.opRevolve","SWEPT_FACE",FACE,{"disambiguationData":[OSD([sQuery(id+"F34.wireOp",EDGE,"E158")])]});
            var sketch = newSketch(context, id + "F36", { "sketchPlane" : qUnion([Q0])});
            skCircle(sketch, "E164", {"center": v(0, 165) * mm, "radius": 24 * mm, "construction": true});
            skLineSegment(sketch, "E165", {"start": v(0, 172) * mm, "end": v(0, 205.8) * mm, "construction": true});
            skPoint(sketch, "E166", {"position": v(0, 189) * mm});
            skCircle(sketch, "E167", {"center": v(0, 189) * mm, "radius": 14 * mm});
            skPoint(sketch, "E168", {"position": v(0, 203) * mm});
            skCircle(sketch, "E169.1.0", {"center": v(-24, 165) * mm, "radius": 14 * mm});
            skCircle(sketch, "E169.2.0", {"center": v(0, 141) * mm, "radius": 14 * mm});
            skCircle(sketch, "E170.1.3.0", {"center": v(24, 165) * mm, "radius": 14 * mm});
            skSolve(sketch);
        }
        {
            var Q0;
            Q0 = qSketchRegion(id + "F36", true);
            extrude(context, id + "F37", {"entities" : qUnion([Q0]), "operationType" : NewBodyOperationType.REMOVE, "endBound" : BoundingType.THROUGH_ALL, "oppositeDirection" : true, "depth" : 25 * mm});
        }
        {
            var Q0;
            Q0=makeQuery(id+"F6.opExtrude","SWEPT_FACE",FACE,{"disambiguationData":[OSD([sQuery(id+"F5.wireOp",EDGE,"E82"),sQuery(id+"F5.wireOp",EDGE,"E84.MirrorCS")])]});
            var sketch = newSketch(context, id + "F38", { "sketchPlane" : qUnion([Q0])});
            skCircle(sketch, "E171", {"center": v(0, 0) * mm, "radius": 1.25 * mm});
            skCircle(sketch, "E172", {"center": v(0, 0) * mm, "radius": 1.5 * mm});
            skSolve(sketch);
        }
        {
            var Q0;
            Q0=makeQuery(id+"F38.imprint","IMPRINT",FACE,{"disambiguationData":[TD([[makeQuery(id+"F38.imprint","IMPRINT",EDGE,{"derivedFrom":sQuery(id+"F38.wireOp",EDGE,"E171")}),1.0]])]});
            extrude(context, id + "F39", {"entities" : qUnion([Q0]), "operationType" : NewBodyOperationType.REMOVE, "endBound" : BoundingType.UP_TO_NEXT, "oppositeDirection" : true, "depth" : 25 * mm});
        }
        {
            var Q0;
            Q0=makeQuery(id+"F38.imprint","IMPRINT",FACE,{"disambiguationData":[TD([[makeQuery(id+"F38.imprint","IMPRINT",EDGE,{"derivedFrom":sQuery(id+"F38.wireOp",EDGE,"E171")}),-1.0]])]});
            extrude(context, id + "F40", {"entities" : qUnion([Q0]), "operationType" : NewBodyOperationType.REMOVE, "oppositeDirection" : true, "depth" : 0.1 * mm});
        }
        {
            var Q0;
            Q0=makeQuery(id+"F6.opExtrude","SWEPT_FACE",FACE,{"disambiguationData":[OSD([sQuery(id+"F5.wireOp",EDGE,"E72"),sQuery(id+"F5.wireOp",EDGE,"E81.MirrorCS")])]});
            var sketch = newSketch(context, id + "F41", { "sketchPlane" : qUnion([Q0])});
            skCircle(sketch, "E173", {"center": v(0, 0) * mm, "radius": 1.5 * mm});
            skSolve(sketch);
        }
        {
            var Q0;
            Q0=makeQuery(id+"F41.imprint","IMPRINT",FACE,{"disambiguationData":[TD([[makeQuery(id+"F41.imprint","IMPRINT",EDGE,{"derivedFrom":sQuery(id+"F41.wireOp",EDGE,"E173")}),1.0]])]});
            extrude(context, id + "F42", {"entities" : qUnion([Q0]), "operationType" : NewBodyOperationType.REMOVE, "oppositeDirection" : true, "depth" : 0.1 * mm});
        }
        {
            var Q0;
            Q0=qCreatedBy(makeId("Front.planeOp"),FACE);
            var sketch = newSketch(context, id + "F43", { "sketchPlane" : qUnion([Q0])});
            skLineSegment(sketch, "E174", {"start": v(50, 52.79) * mm, "end": v(50, -16.82) * mm, "construction": true});
            skLineSegment(sketch, "E175", {"start": v(50, 8) * mm, "end": v(0, 8) * mm, "construction": true});
            skLineSegment(sketch, "E176.bottom", {"start": v(31, 6) * mm, "end": v(39, 6) * mm, "construction": true});
            skLineSegment(sketch, "E176.top", {"start": v(31, -6) * mm, "end": v(39, -6) * mm, "construction": true});
            skLineSegment(sketch, "E176.left", {"start": v(31, 6) * mm, "end": v(31, -6) * mm, "construction": true});
            skLineSegment(sketch, "E176.right", {"start": v(39, 6) * mm, "end": v(39, -6) * mm, "construction": true});
            skLineSegment(sketch, "E177", {"start": v(50, 0) * mm, "end": v(31, 6) * mm, "construction": true});
            skLineSegment(sketch, "E178", {"start": v(50, 0) * mm, "end": v(31.75, 8) * mm, "construction": true});
            skLineSegment(sketch, "E179", {"start": v(50, 0) * mm, "end": v(0, 0) * mm, "construction": true});
            skLineSegment(sketch, "E180", {"start": v(0, 0) * mm, "end": v(31, 6) * mm, "construction": true});
            skLineSegment(sketch, "E181", {"start": v(50, 0) * mm, "end": v(0.29, 5.35) * mm, "construction": true});
            skLineSegment(sketch, "E182", {"start": v(0.29, 5.35) * mm, "end": v(31.75, 8) * mm, "construction": true});
            skLineSegment(sketch, "E183", {"start": v(0.29, 5.35) * mm, "end": v(0.93, 11.32) * mm, "construction": true});
            skLineSegment(sketch, "E184", {"start": v(0.93, 11.32) * mm, "end": v(50.64, 5.97) * mm, "construction": true});
            skLineSegment(sketch, "E185", {"start": v(50.64, 5.97) * mm, "end": v(50, 0) * mm, "construction": true});
            skLineSegment(sketch, "E186", {"start": v(37.35, 10.41) * mm, "end": v(32.07, 10.98) * mm});
            skLineSegment(sketch, "E187", {"start": v(32.07, 10.98) * mm, "end": v(31.75, 8) * mm});
            skLineSegment(sketch, "E188", {"start": v(31.75, 8) * mm, "end": v(37.03, 7.43) * mm});
            skArc(sketch, "E189", {"start": v(44, 10) * mm, "mid": v(42.86, 9.77) * mm, "end": v(41.89, 9.13) * mm});
            skArc(sketch, "E190", {"start": v(37.03, 7.43) * mm, "mid": v(39.65, 7.73) * mm, "end": v(41.89, 9.13) * mm});
            skLineSegment(sketch, "E191", {"start": v(44, 10) * mm, "end": v(50, 10) * mm, "construction": true});
            skArc(sketch, "E192", {"start": v(44, 13) * mm, "mid": v(41.72, 12.55) * mm, "end": v(39.78, 11.26) * mm});
            skArc(sketch, "E193", {"start": v(37.35, 10.41) * mm, "mid": v(38.66, 10.57) * mm, "end": v(39.78, 11.26) * mm});
            skSolve(sketch);
        }
        {
            var Q0;
            Q0=qCreatedBy(makeId("Front.planeOp"),FACE);
            var sketch = newSketch(context, id + "F44", { "sketchPlane" : qUnion([Q0])});
            skLineSegment(sketch, "E194.bottom", {"start": v(44, 13) * mm, "end": v(31, 13) * mm});
            skLineSegment(sketch, "E194.top", {"start": v(44, 10) * mm, "end": v(31, 10) * mm});
            skLineSegment(sketch, "E194.left", {"start": v(44, 13) * mm, "end": v(44, 10) * mm});
            skLineSegment(sketch, "E194.right", {"start": v(31, 13) * mm, "end": v(31, 10) * mm});
            skLineSegment(sketch, "E195.bottom", {"start": v(31, 13) * mm, "end": v(34, 13) * mm});
            skLineSegment(sketch, "E195.top", {"start": v(31, 41) * mm, "end": v(34, 41) * mm});
            skLineSegment(sketch, "E195.left", {"start": v(31, 13) * mm, "end": v(31, 41) * mm});
            skLineSegment(sketch, "E195.right", {"start": v(34, 13) * mm, "end": v(34, 41) * mm});
            skSolve(sketch);
        }
        {
            var Q0;
            Q0 = qSketchRegion(id + "F44", true);
            extrude(context, id + "F45", {"entities" : qUnion([Q0]), "operationType" : NewBodyOperationType.ADD, "endBound" : BoundingType.SYMMETRIC, "depth" : 20 * mm});
        }
        {
            var Q0;
            Q0=makeQuery(id+"F6.opExtrude","CAP_FACE",FACE,{"disambiguationData":[OSD([sQuery(id+"F5.wireOp",EDGE,"E64"),sQuery(id+"F5.wireOp",EDGE,"E65"),sQuery(id+"F5.wireOp",EDGE,"E66"),sQuery(id+"F5.wireOp",EDGE,"E67"),sQuery(id+"F5.wireOp",EDGE,"E68"),sQuery(id+"F5.wireOp",EDGE,"E69"),sQuery(id+"F5.wireOp",EDGE,"E71"),sQuery(id+"F5.wireOp",EDGE,"E72"),sQuery(id+"F5.wireOp",EDGE,"E73.filletArc"),sQuery(id+"F5.wireOp",EDGE,"E74.MirrorCS"),sQuery(id+"F5.wireOp",EDGE,"E75.MirrorCS"),sQuery(id+"F5.wireOp",EDGE,"E76.MirrorCS"),sQuery(id+"F5.wireOp",EDGE,"E77.MirrorCS"),sQuery(id+"F5.wireOp",EDGE,"E78.MirrorCS"),sQuery(id+"F5.wireOp",EDGE,"E79.MirrorCS"),sQuery(id+"F5.wireOp",EDGE,"E80.MirrorCS"),sQuery(id+"F5.wireOp",EDGE,"E81.MirrorCS"),sQuery(id+"F5.wireOp",EDGE,"E82"),sQuery(id+"F5.wireOp",EDGE,"E83.filletArc"),sQuery(id+"F5.wireOp",EDGE,"E84.MirrorCS"),sQuery(id+"F5.wireOp",EDGE,"E85.MirrorCS"),sQuery(id+"F5.wireOp",EDGE,"E86.MirrorCS")])],"isStart":false});
            var sketch = newSketch(context, id + "F46", { "sketchPlane" : qUnion([Q0])});
            skLineSegment(sketch, "E196.bottom", {"start": v(33, 27.5) * mm, "end": v(37, 27.5) * mm});
            skLineSegment(sketch, "E196.top", {"start": v(33, -27.5) * mm, "end": v(37, -27.5) * mm});
            skLineSegment(sketch, "E196.left", {"start": v(31, 25.5) * mm, "end": v(31, -25.5) * mm});
            skLineSegment(sketch, "E196.right", {"start": v(39, 25.5) * mm, "end": v(39, -25.5) * mm});
            skPoint(sketch, "E197", {"position": v(39, 0) * mm});
            skLineSegment(sketch, "E198", {"start": v(35, 27.5) * mm, "end": v(35, -27.5) * mm, "construction": true});
            skCircle(sketch, "E199", {"center": v(35, 23.5) * mm, "radius": 1.75 * mm});
            skCircle(sketch, "E200", {"center": v(35, -23.5) * mm, "radius": 1.75 * mm});
            skPoint(sketch, "E201.visualSharp", {"position": v(31, 27.5) * mm});
            skArc(sketch, "E201.filletArc", {"start": v(33, 27.5) * mm, "mid": v(31.59, 26.91) * mm, "end": v(31, 25.5) * mm});
            skPoint(sketch, "E202.visualSharp", {"position": v(39, 27.5) * mm});
            skArc(sketch, "E202.filletArc", {"start": v(39, 25.5) * mm, "mid": v(38.41, 26.91) * mm, "end": v(37, 27.5) * mm});
            skPoint(sketch, "E203.visualSharp", {"position": v(39, -27.5) * mm});
            skArc(sketch, "E203.filletArc", {"start": v(37, -27.5) * mm, "mid": v(38.41, -26.91) * mm, "end": v(39, -25.5) * mm});
            skPoint(sketch, "E204.visualSharp", {"position": v(31, -27.5) * mm});
            skArc(sketch, "E204.filletArc", {"start": v(31, -25.5) * mm, "mid": v(31.59, -26.91) * mm, "end": v(33, -27.5) * mm});
            skSolve(sketch);
        }
        {
            var Q0;
            Q0 = qSketchRegion(id + "F46", true);
            extrude(context, id + "F47", {"entities" : qUnion([Q0]), "depth" : 2 * mm});
        }
        {
            var Q0;
            Q0=makeQuery(id+"F45.opExtrude","SWEPT_EDGE",EDGE,{"disambiguationData":[OSD([sQuery(id+"F44.wireOp",EDGE,"E194.top"),sQuery(id+"F44.wireOp",EDGE,"E194.right")])]});
            fillet(context, id + "F48", {"entities" : qUnion([Q0]), "radius" : 6 * mm, "tangentPropagation" : true, "allowEdgeOverflow" : false});
        }
        {
            var Q0;
            Q0=makeQuery(id+"F45.opExtrude","SWEPT_EDGE",EDGE,{"disambiguationData":[OSD([sQuery(id+"F44.wireOp",EDGE,"E194.bottom"),sQuery(id+"F44.wireOp",EDGE,"E195.bottom"),sQuery(id+"F44.wireOp",EDGE,"E195.right")])]});
            fillet(context, id + "F49", {"entities" : qUnion([Q0]), "radius" : 3 * mm, "tangentPropagation" : true, "allowEdgeOverflow" : false});
        }
        {
            var Q0;
            Q0=makeQuery(id+"F45.opExtrude","SWEPT_FACE",FACE,{"disambiguationData":[OSD([sQuery(id+"F44.wireOp",EDGE,"E194.right"),sQuery(id+"F44.wireOp",EDGE,"E195.left")])]});
            var sketch = newSketch(context, id + "F50", { "sketchPlane" : qUnion([Q0])});
            skCircle(sketch, "E205", {"center": v(0, 21) * mm, "radius": 1.65 * mm});
            skCircle(sketch, "E206.0.1.0", {"center": v(0, 28.5) * mm, "radius": 1.65 * mm});
            skCircle(sketch, "E206.0.2.0", {"center": v(0, 36) * mm, "radius": 1.65 * mm});
            skLineSegment(sketch, "E206.direction1", {"start": v(0, 21) * mm, "end": v(26.3, 21) * mm, "construction": true});
            skLineSegment(sketch, "E206.direction2", {"start": v(0, 21) * mm, "end": v(0, 28.5) * mm, "construction": true});
            skSolve(sketch);
        }
        {
            var Q0;
            Q0 = qSketchRegion(id + "F50", true);
            extrude(context, id + "F51", {"entities" : qUnion([Q0]), "operationType" : NewBodyOperationType.REMOVE, "endBound" : BoundingType.THROUGH_ALL, "oppositeDirection" : true, "depth" : 25 * mm});
        }
        {
            var Q0;
            Q0=makeQuery(id+"F15.opExtrude","SWEPT_FACE",FACE,{"disambiguationData":[OSD([sQuery(id+"F14.wireOp",EDGE,"E113")])]});
            var sketch = newSketch(context, id + "F52", { "sketchPlane" : qUnion([Q0])});
            skLineSegment(sketch, "E207", {"start": v(18.8, -56) * mm, "end": v(18.8, -57) * mm});
            skLineSegment(sketch, "E208", {"start": v(12.8, -63) * mm, "end": v(1.8, -63) * mm});
            skLineSegment(sketch, "E209", {"start": v(-18.8, -57) * mm, "end": v(-18.8, -56) * mm});
            skLineSegment(sketch, "E210", {"start": v(-18.8, -56) * mm, "end": v(-15.8, -56) * mm});
            skLineSegment(sketch, "E211", {"start": v(-15.8, -56) * mm, "end": v(-15.8, -57) * mm});
            skLineSegment(sketch, "E212", {"start": v(-12.8, -60) * mm, "end": v(-1.8, -60) * mm});
            skLineSegment(sketch, "E213", {"start": v(15.8, -57) * mm, "end": v(15.8, -56) * mm});
            skLineSegment(sketch, "E214", {"start": v(15.8, -56) * mm, "end": v(18.8, -56) * mm});
            skLineSegment(sketch, "E215.left", {"start": v(1.8, -60) * mm, "end": v(1.8, -63) * mm});
            skLineSegment(sketch, "E215.right", {"start": v(-1.8, -60) * mm, "end": v(-1.8, -63) * mm});
            skPoint(sketch, "E216.visualSharp", {"position": v(15.8, -60) * mm});
            skArc(sketch, "E216.filletArc", {"start": v(12.8, -60) * mm, "mid": v(14.92, -59.12) * mm, "end": v(15.8, -57) * mm});
            skPoint(sketch, "E217.visualSharp", {"position": v(-15.8, -60) * mm});
            skArc(sketch, "E217.filletArc", {"start": v(-15.8, -57) * mm, "mid": v(-14.92, -59.12) * mm, "end": v(-12.8, -60) * mm});
            skPoint(sketch, "E218.visualSharp", {"position": v(18.8, -63) * mm});
            skArc(sketch, "E218.filletArc", {"start": v(12.8, -63) * mm, "mid": v(17.04, -61.24) * mm, "end": v(18.8, -57) * mm});
            skPoint(sketch, "E219.visualSharp", {"position": v(-18.8, -63) * mm});
            skArc(sketch, "E219.filletArc", {"start": v(-18.8, -57) * mm, "mid": v(-17.04, -61.24) * mm, "end": v(-12.8, -63) * mm});
            skLineSegment(sketch, "E220.trimOffspring", {"start": v(-1.8, -63) * mm, "end": v(-12.8, -63) * mm});
            skLineSegment(sketch, "E221.trimOffspring", {"start": v(1.8, -60) * mm, "end": v(12.8, -60) * mm});
            skPoint(sketch, "E222", {"position": v(0, -63) * mm});
            skSolve(sketch);
        }
        {
            var Q0;
            Q0 = qSketchRegion(id + "F52", true);
            extrude(context, id + "F53", {"entities" : qUnion([Q0]), "operationType" : NewBodyOperationType.ADD, "oppositeDirection" : true, "depth" : 30 * mm});
        }
    });
